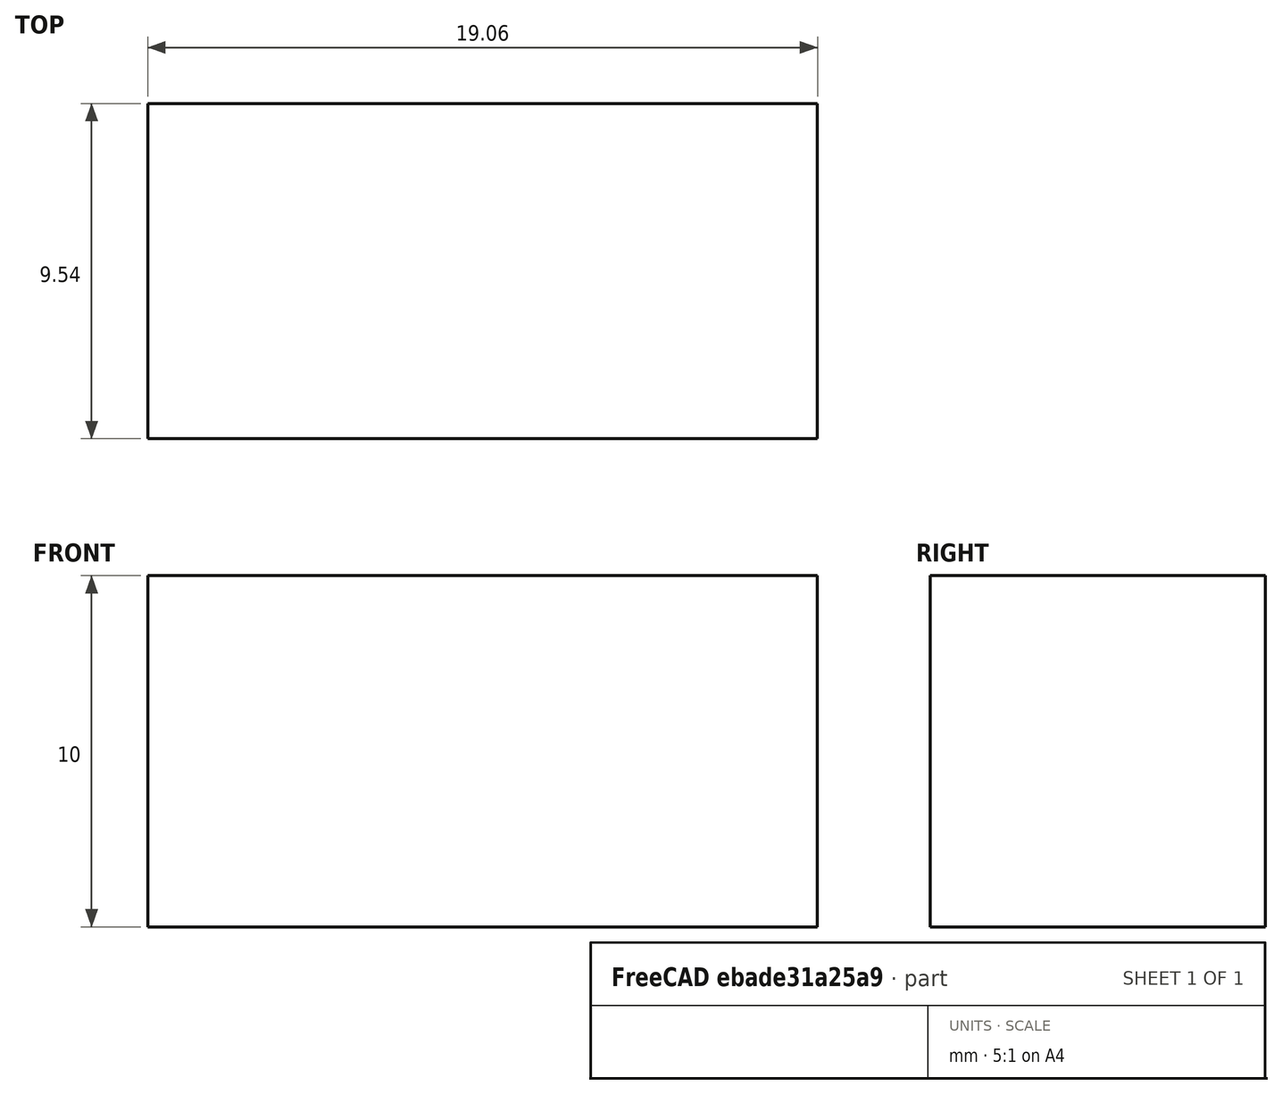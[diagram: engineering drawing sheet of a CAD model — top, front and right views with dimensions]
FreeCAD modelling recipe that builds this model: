
FCSTD DOCUMENT  (FreeCAD 0.21R39043 (Git))
Label: waveguide1
License: All rights reserved
LicenseURL: https://en.wikipedia.org/wiki/All_rights_reserved
objects: PartDesign::Body×3, Sketcher::SketchObject×2, PartDesign::Pad×1, PartDesign::SubShapeBinder×1, Part::SubShapeBinder×1, PartDesign::Extrusion×1, App::Part×1
note: 15 computed .brp shape members not serialized (recipe doc carries the construction recipe); baked Part::Feature solids carry a one-line shape summary decoded from their .brp
EXTERNAL_REF file=test.FCStd obj=Assembly

FEATURE [Sketcher::SketchObject] Sketch
  ArcFitTolerance = 1e-06
  AttachmentSupport = -> [XZ_Plane]
  ExternalBSplineMaxDegree = 5
  ExternalBSplineTolerance = 0.0001
  FixShape = 1
  FullyConstrained = true
  InternalTolerance = 1e-06
  InvalidShape = false
  MakeInternals = false
  MapMode = 5
  Placement = pos=(0,0,0) rot=(1,0,0;1.5708rad)
  Support = -> [XZ_Plane]
  TreeRank = 14
  ValidateShape = false
  sketch-geometry (4):
    g0: LineSegment StartX=-9.525 StartY=5 StartZ=0 EndX=9.525 EndY=5 EndZ=0
    g1: LineSegment StartX=9.525 StartY=5 StartZ=0 EndX=9.525 EndY=-5 EndZ=0
    g2: LineSegment StartX=9.525 StartY=-5 StartZ=0 EndX=-9.525 EndY=-5 EndZ=0
    g3: LineSegment StartX=-9.525 StartY=-5 StartZ=0 EndX=-9.525 EndY=5 EndZ=0
  constraints (11):
    c: Coincident(g0,g1)
    c: Coincident(g1,g2)
    c: Coincident(g2,g3)
    c: Coincident(g3,g0)
    c: Horizontal(g0)
    c: Horizontal(g2)
    c: Vertical(g1)
    c: DistanceY(g3,g3) = 10
    c: DistanceX(g2,g2) = 19.05
    c: Vertical(g3)
    c: Symmetric(g0,g2,g-1)
FEATURE [PartDesign::Pad] Pad
  AddSubType = 0
  AlongSketchNormal = false
  AutoTaperInnerAngle = true
  CheckUpToFaceLimits = true
  ClaimChildren = false
  Direction = (0,-1,0)
  Fit = 0
  FitJoin = 0
  FixShape = 1
  InnerFit = 0
  InnerFitJoin = 0
  InvalidShape = false
  Length = 9.54
  Length2 = 10
  Linearize = true
  NewSolid = false
  Profile = -> Sketch
  ReferenceAxis = -> Sketch [N_Axis]
  Suppress = false
  TaperInnerAngle = 0
  TaperInnerAngleRev = 0
  TreeRank = 15
  Type = 0
  ValidateShape = true
  _ProfileBasedVersion = 1
FEATURE [PartDesign::Body] Body  label="DIEL_CAVITY"
  AutoGroupSolids = false
  ClaimAllChildren = false
  ExportMode = 0
  FixShape = 1
  Group = -> [Sketch,Pad]
  InvalidShape = false
  Origin = -> Origin001
  Tip = -> Pad
  TreeRank = 13
  ValidateShape = false
  _ExportChildren = -> [Pad]
  _GroupVersion = 1
FEATURE [PartDesign::SubShapeBinder] Binder  label="Binder(Pad)"
  BindCopyOnChange = 0
  BindMode = 0
  ClaimChildren = false
  Context = -> Part [Body001.Binder.]
  EdgeTolerance = 1e-06
  FillStyle = 0
  FixShape = 1
  Fuse = false
  Group_EnableExport = true
  InvalidShape = false
  MakeFace = true
  MergeEdges = true
  OffsetFill = false
  OffsetIntersection = false
  OffsetJoinType = 0
  OffsetOpenResult = false
  Outline = false
  PartialLoad = false
  Relative = true
  SplitEdges = false
  Support = -> [Body[Pad.Face3]]
  TightBound = false
  TreeRank = 37
  ValidateShape = false
  _Version = 8
FEATURE [PartDesign::Body] Body001  label="WGP_1"
  AutoGroupSolids = false
  ClaimAllChildren = false
  ExportMode = 2
  FixShape = 1
  Group = -> [Binder]
  InvalidShape = false
  Origin = -> Origin002
  TreeRank = 25
  ValidateShape = false
  _ExportChildren = -> [Binder]
  _GroupVersion = 1
FEATURE [Part::SubShapeBinder] Import  label="Import(Pad)"
  BindCopyOnChange = 0
  BindMode = 0
  ClaimChildren = false
  Context = -> <external test.FCStd>#Assembly [Parts.Link.Body002.Import.]
  EdgeTolerance = 1e-06
  FillStyle = 0
  FixShape = 1
  Fuse = false
  Group_EnableExport = false
  InvalidShape = false
  MakeFace = false
  MergeEdges = true
  OffsetFill = false
  OffsetIntersection = false
  OffsetJoinType = 0
  OffsetOpenResult = false
  Outline = false
  PartialLoad = false
  Relative = true
  SplitEdges = false
  Support = -> [Body[Pad.]]
  TightBound = false
  TreeRank = 49
  ValidateShape = false
  _Version = 8
FEATURE [Sketcher::SketchObject] Sketch001
  ArcFitTolerance = 1e-06
  AttachmentSupport = -> [XZ_Plane002]
  ExternalBSplineMaxDegree = 5
  ExternalBSplineTolerance = 0.0001
  ExternalGeometry = -> [Import]
  FixShape = 1
  FullyConstrained = true
  Group_EnableExport = false
  InternalTolerance = 1e-06
  InvalidShape = false
  MakeInternals = false
  MapMode = 5
  Placement = pos=(0,0,0) rot=(1,0,0;1.5708rad)
  Support = -> [XZ_Plane002]
  TreeRank = 48
  ValidateShape = false
  sketch-geometry (1):
    g0: LineSegment StartX=-9.525 StartY=0 StartZ=0 EndX=9.525 EndY=0 EndZ=0
  constraints (4):
    c: PointOnObject(g0,g-3)
    c: PointOnObject(g0,g-4)
    c: Horizontal(g0)
    c: PointOnObject(g-1,g0)
FEATURE [PartDesign::Extrusion] Extrusion
  AddSubType = 0
  AlongSketchNormal = false
  AutoTaperInnerAngle = true
  CheckUpToFaceLimits = true
  ClaimChildren = false
  Direction = (0,-1,2e-16)
  Fit = 0
  FitJoin = 0
  FixShape = 1
  Group_EnableExport = true
  InnerFit = 0
  InnerFitJoin = 0
  InvalidShape = false
  Length = 9.54
  Length2 = 10
  Linearize = true
  NewSolid = false
  Profile = -> Sketch001
  ReferenceAxis = -> Sketch001 [N_Axis]
  Suppress = false
  TaperInnerAngle = 0
  TaperInnerAngleRev = 0
  TreeRank = 50
  Type = 0
  ValidateShape = true
  _ProfileBasedVersion = 1
FEATURE [PartDesign::Body] Body002  label="SPLIT_1"
  AutoGroupSolids = false
  ClaimAllChildren = false
  ExportMode = 2
  FixShape = 1
  Group = -> [Sketch001,Import,Extrusion]
  InvalidShape = false
  Origin = -> Origin003
  TreeRank = 47
  ValidateShape = false
  _ExportChildren = -> [Sketch001,Import,Extrusion]
  _GroupVersion = 1
FEATURE [App::Part] Part  label="CMP_waveguide1"
  ClaimAllChildren = false
  ExportMode = 1
  Group = -> [Body,Body001,Body002]
  Origin = -> Origin
  TreeRank = 3
  _ExportChildren = -> [Body,Body001,Body002]
  _GroupVersion = 1
